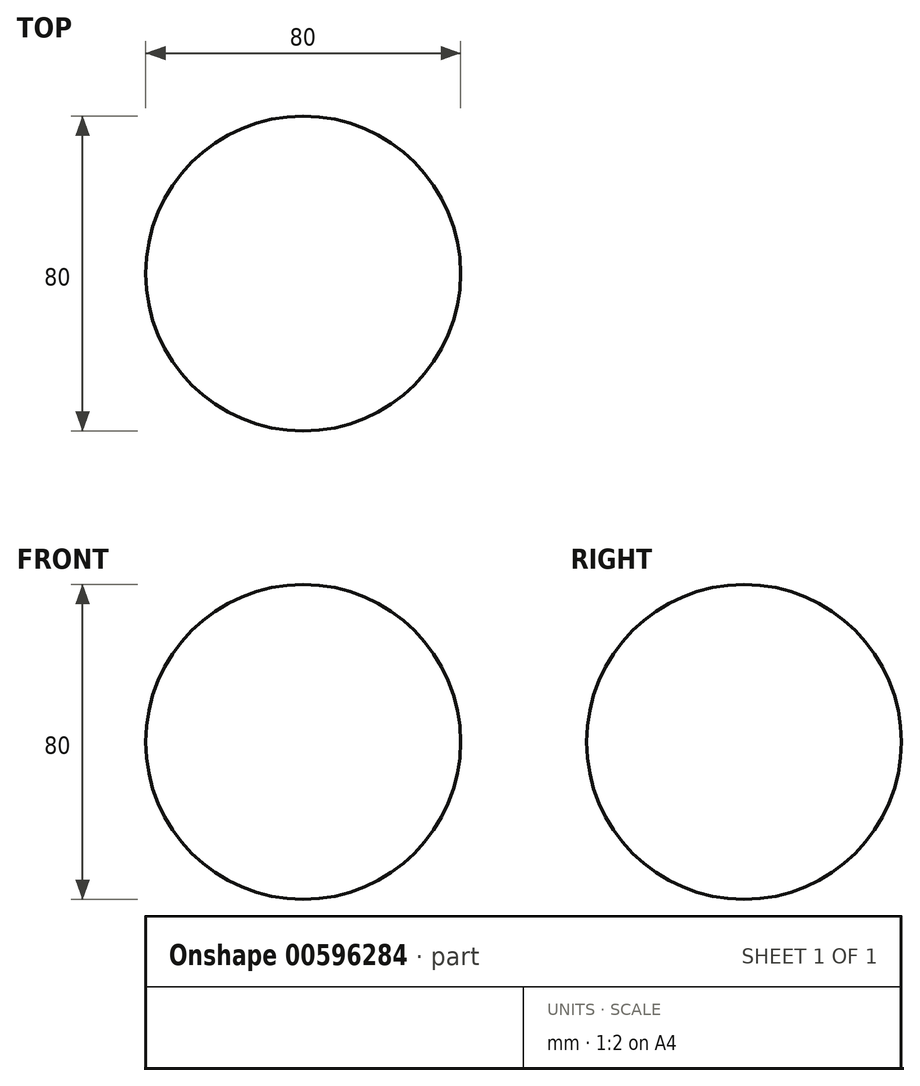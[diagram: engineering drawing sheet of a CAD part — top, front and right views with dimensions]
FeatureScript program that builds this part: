
annotation { "Feature Type Name" : "Feature", "Feature Type Description" : "" }
export const myFeature = defineFeature(function(context is Context, id is Id, definition is map)
    precondition{}
    {
        {
            var Q0;
            Q0=qCreatedBy(makeId("Front.planeOp"),FACE);
            var sketch = newSketch(context, id + "F0", { "sketchPlane" : qUnion([Q0])});
            skArc(sketch, "E0", {"start": v(0, -40) * mm, "mid": v(40, 0) * mm, "end": v(0, 40) * mm});
            skLineSegment(sketch, "E1", {"start": v(0, 40) * mm, "end": v(0, -40) * mm});
            skSolve(sketch);
        }
        {
            var Q0;
            Q0=qCreatedBy(makeId("Front.planeOp"),FACE);
            var sketch = newSketch(context, id + "F1", { "sketchPlane" : qUnion([Q0])});
            skLineSegment(sketch, "E2", {"start": v(0, 45.55) * mm, "end": v(0, -45.84) * mm});
            skSolve(sketch);
        }
        {
            var Q0;
            Q0 = qSketchRegion(id + "F0", true);
            var Q1;
            Q1=sQuery(id+"F1.wireOp",EDGE,"E2");
            revolve(context, id + "F2", {"entities" : qUnion([Q0]), "axis" : qUnion([Q1]), "revolveType" : RevolveType.FULL});
        }
    });
